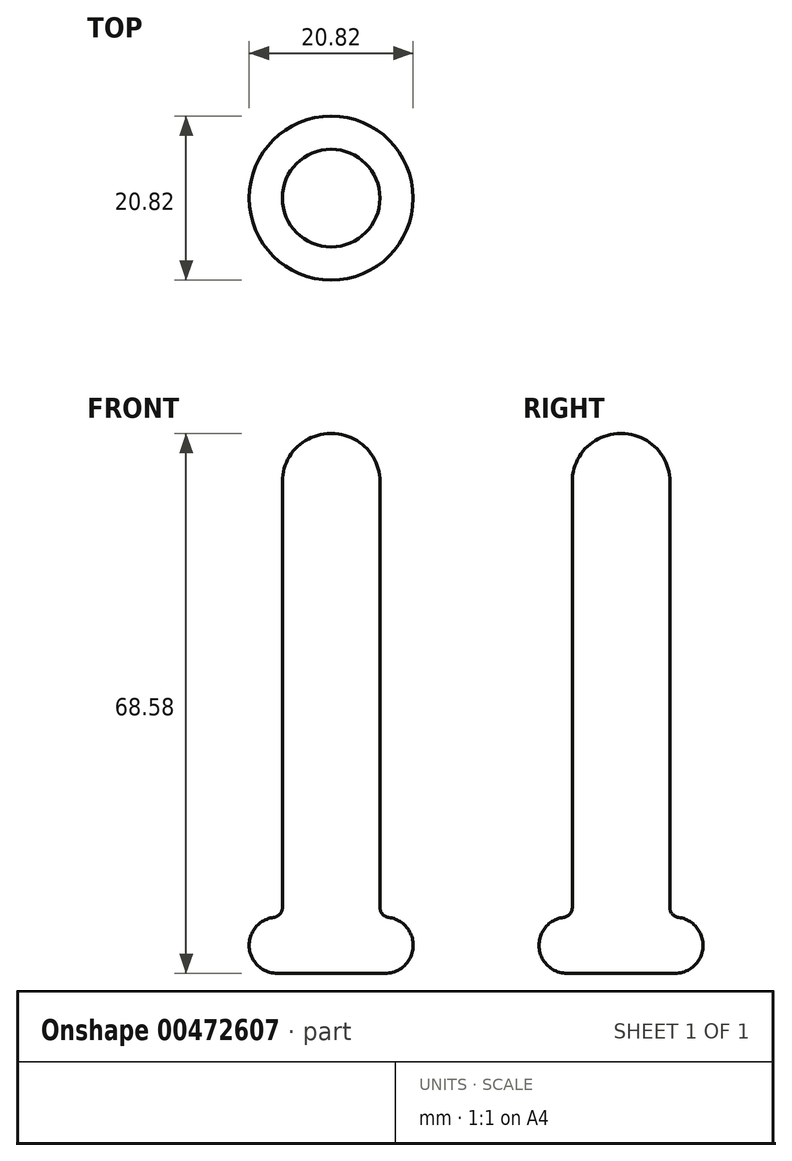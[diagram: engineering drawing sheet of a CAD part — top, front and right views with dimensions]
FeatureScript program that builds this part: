
annotation { "Feature Type Name" : "Feature", "Feature Type Description" : "" }
export const myFeature = defineFeature(function(context is Context, id is Id, definition is map)
    precondition{}
    {
        {
            var Q0;
            Q0=qCreatedBy(makeId("Front.planeOp"),FACE);
            var sketch = newSketch(context, id + "F0", { "sketchPlane" : qUnion([Q0])});
            skLineSegment(sketch, "E0", {"start": v(0, 0) * mm, "end": v(-6.86, 0) * mm});
            skLineSegment(sketch, "E1", {"start": v(-10.41, 3.56) * mm, "end": v(-10.41, 3.58) * mm});
            skLineSegment(sketch, "E2", {"start": v(-0.1, 68.58) * mm, "end": v(0, 68.58) * mm});
            skLineSegment(sketch, "E3", {"start": v(0, 68.58) * mm, "end": v(0, 0) * mm});
            skPoint(sketch, "E4.visualSharp", {"position": v(-6.1, 68.58) * mm});
            skArc(sketch, "E4.filletArc", {"start": v(-0.1, 68.58) * mm, "mid": v(-4.41, 66.8) * mm, "end": v(-6.2, 62.48) * mm});
            skPoint(sketch, "E5.visualSharp", {"position": v(-10.41, 7.11) * mm});
            skPoint(sketch, "E6.visualSharp", {"position": v(-10.41, 0) * mm});
            skLineSegment(sketch, "E7.trimOffspring", {"start": v(-6.2, 8.37) * mm, "end": v(-6.2, 62.48) * mm});
            skPoint(sketch, "E8.visualSharp", {"position": v(-6.2, 7.11) * mm});
            skArc(sketch, "E9.filletArc", {"start": v(-7.3, 7.11) * mm, "mid": v(-9.53, 5.93) * mm, "end": v(-10.41, 3.58) * mm});
            skArc(sketch, "E10.filletArc", {"start": v(-10.41, 3.56) * mm, "mid": v(-9.37, 1.04) * mm, "end": v(-6.86, 0) * mm});
            skArc(sketch, "E11.filletArc", {"start": v(-7.3, 7.11) * mm, "mid": v(-6.51, 7.53) * mm, "end": v(-6.2, 8.37) * mm});
            skSolve(sketch);
        }
        {
            var Q0;
            Q0=makeQuery(id+"F0.imprint","IMPRINT",FACE,{"disambiguationData":[TD([[makeQuery(id+"F0.imprint","IMPRINT",EDGE,{"derivedFrom":sQuery(id+"F0.wireOp",EDGE,"E0")}),-1.0]])]});
            var Q1;
            Q1=sQuery(id+"F0.wireOp",EDGE,"E3");
            revolve(context, id + "F1", {"entities" : qUnion([Q0]), "axis" : qUnion([Q1]), "revolveType" : RevolveType.FULL});
        }
    });
